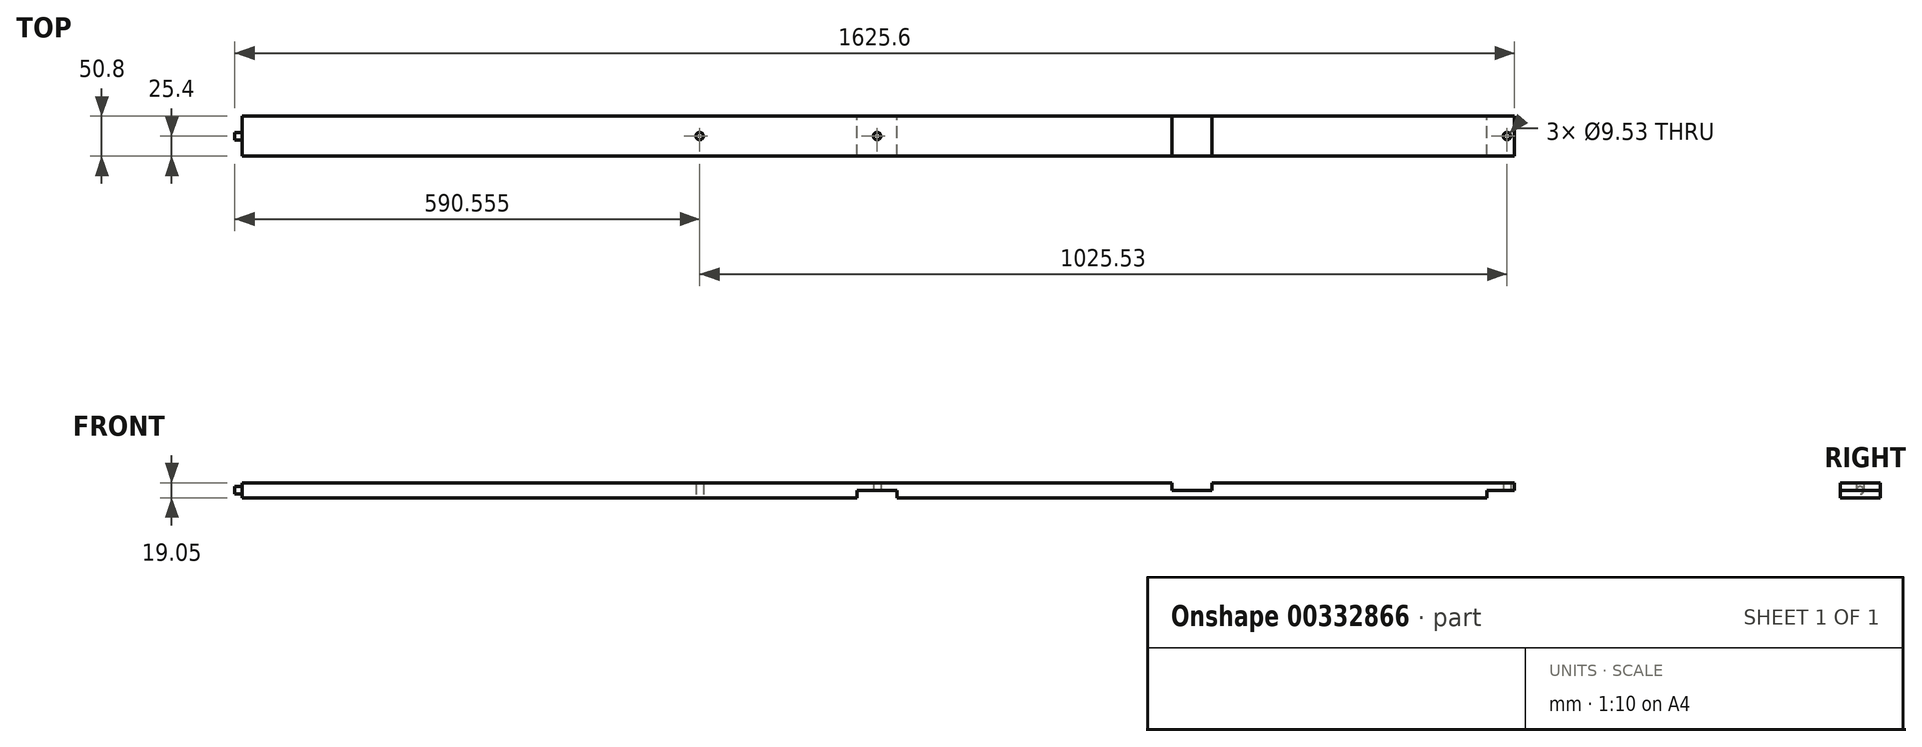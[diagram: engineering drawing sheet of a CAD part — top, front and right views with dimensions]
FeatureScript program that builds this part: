
annotation { "Feature Type Name" : "Feature", "Feature Type Description" : "" }
export const myFeature = defineFeature(function(context is Context, id is Id, definition is map)
    precondition{}
    {
        {
            var Q0;
            Q0=qCreatedBy(makeId("Front.planeOp"),FACE);
            var sketch = newSketch(context, id + "F0", { "sketchPlane" : qUnion([Q0])});
            skLineSegment(sketch, "E0", {"start": v(1616.08, 19.05) * mm, "end": v(0, 19.05) * mm});
            skPoint(sketch, "E1.left.start.orphan", {"position": v(-798.41, -3.82) * mm});
            skLineSegment(sketch, "E2.top", {"start": v(781.05, 9.52) * mm, "end": v(831.85, 9.52) * mm});
            skLineSegment(sketch, "E2.left", {"start": v(781.05, 0) * mm, "end": v(781.05, 9.52) * mm});
            skLineSegment(sketch, "E2.right", {"start": v(831.85, 0) * mm, "end": v(831.85, 9.52) * mm});
            skLineSegment(sketch, "E3.trimOffspring", {"start": v(831.85, 0) * mm, "end": v(1581.15, 0) * mm});
            skLineSegment(sketch, "E4.left", {"start": v(1581.15, 0) * mm, "end": v(1581.15, 9.53) * mm});
            skLineSegment(sketch, "E5.trimOffspring", {"start": v(939.8, 0) * mm, "end": v(939.8, 0) * mm});
            skLineSegment(sketch, "E6.top", {"start": v(1581.15, 9.52) * mm, "end": v(1616.08, 9.52) * mm});
            skPoint(sketch, "E7.orphan", {"position": v(1631.95, 0) * mm});
            skLineSegment(sketch, "E8", {"start": v(0, 0) * mm, "end": v(0, 19.05) * mm});
            skLineSegment(sketch, "E9", {"start": v(781.05, 0) * mm, "end": v(0, 0) * mm});
            skLineSegment(sketch, "E10", {"start": v(1616.08, 19.05) * mm, "end": v(1616.08, 9.53) * mm});
            skSolve(sketch);
        }
        {
            var Q0;
            Q0=qSketchRegion(id+"F0",true);
            extrude(context, id + "F1", {"entities" : qUnion([Q0]), "depth" : 50.8 * mm});
        }
        {
            var Q0;
            Q0=qCreatedBy(makeId("Top.planeOp"),FACE);
            cPlane(context, id + "F2", {"entities" : qUnion([Q0]), "cplaneType" : CPlaneType.OFFSET, "offset" : 9.52 * mm, "width" : 152.4 * mm, "height" : 152.4 * mm});
        }
        {
            var Q0;
            Q0=qCreatedBy(id+"F2.planeOp",FACE);
            var sketch = newSketch(context, id + "F3", { "sketchPlane" : qUnion([Q0])});
            skCircle(sketch, "E11", {"center": v(806.45, -25.4) * mm, "radius": 4.76 * mm});
            skCircle(sketch, "E12", {"center": v(1606.55, -25.4) * mm, "radius": 4.76 * mm});
            skCircle(sketch, "E13", {"center": v(581.02, -25.4) * mm, "radius": 4.76 * mm});
            skSolve(sketch);
        }
        {
            var Q0;
            Q0=qSketchRegion(id+"F3",true);
            extrude(context, id + "F4", {"entities" : qUnion([Q0]), "operationType" : NewBodyOperationType.REMOVE, "endBound" : BoundingType.SYMMETRIC, "depth" : 25.4 * mm});
        }
        {
            var Q0;
            Q0=qCreatedBy(makeId("Right.planeOp"),FACE);
            var sketch = newSketch(context, id + "F5", { "sketchPlane" : qUnion([Q0])});
            skCircle(sketch, "E14", {"center": v(-25.4, 9.53) * mm, "radius": 4.76 * mm});
            skSolve(sketch);
        }
        {
            var Q0;
            Q0=qSketchRegion(id+"F5",true);
            extrude(context, id + "F6", {"entities" : qUnion([Q0]), "operationType" : NewBodyOperationType.ADD, "oppositeDirection" : true, "depth" : 9.52 * mm});
        }
        {
            var Q0;
            Q0=qCreatedBy(id+"F2.planeOp",FACE);
            var sketch = newSketch(context, id + "F7", { "sketchPlane" : qUnion([Q0])});
            skLineSegment(sketch, "E15", {"start": v(1206.5, 250.52) * mm, "end": v(1206.5, -231.12) * mm, "construction": true});
            skLineSegment(sketch, "E16.bottom", {"start": v(1181.1, -89.63) * mm, "end": v(1231.9, -89.63) * mm});
            skLineSegment(sketch, "E16.top", {"start": v(1181.1, 30.31) * mm, "end": v(1231.9, 30.31) * mm});
            skLineSegment(sketch, "E16.left", {"start": v(1181.1, -89.63) * mm, "end": v(1181.1, 30.31) * mm});
            skLineSegment(sketch, "E16.right", {"start": v(1231.9, -89.63) * mm, "end": v(1231.9, 30.31) * mm});
            skPoint(sketch, "E16.middle", {"position": v(1206.5, -29.66) * mm});
            skSolve(sketch);
        }
        {
            var Q0;
            Q0 = qSketchRegion(id + "F7", true);
            extrude(context, id + "F8", {"entities" : qUnion([Q0]), "operationType" : NewBodyOperationType.REMOVE, "depth" : 25.4 * mm});
        }
    });
